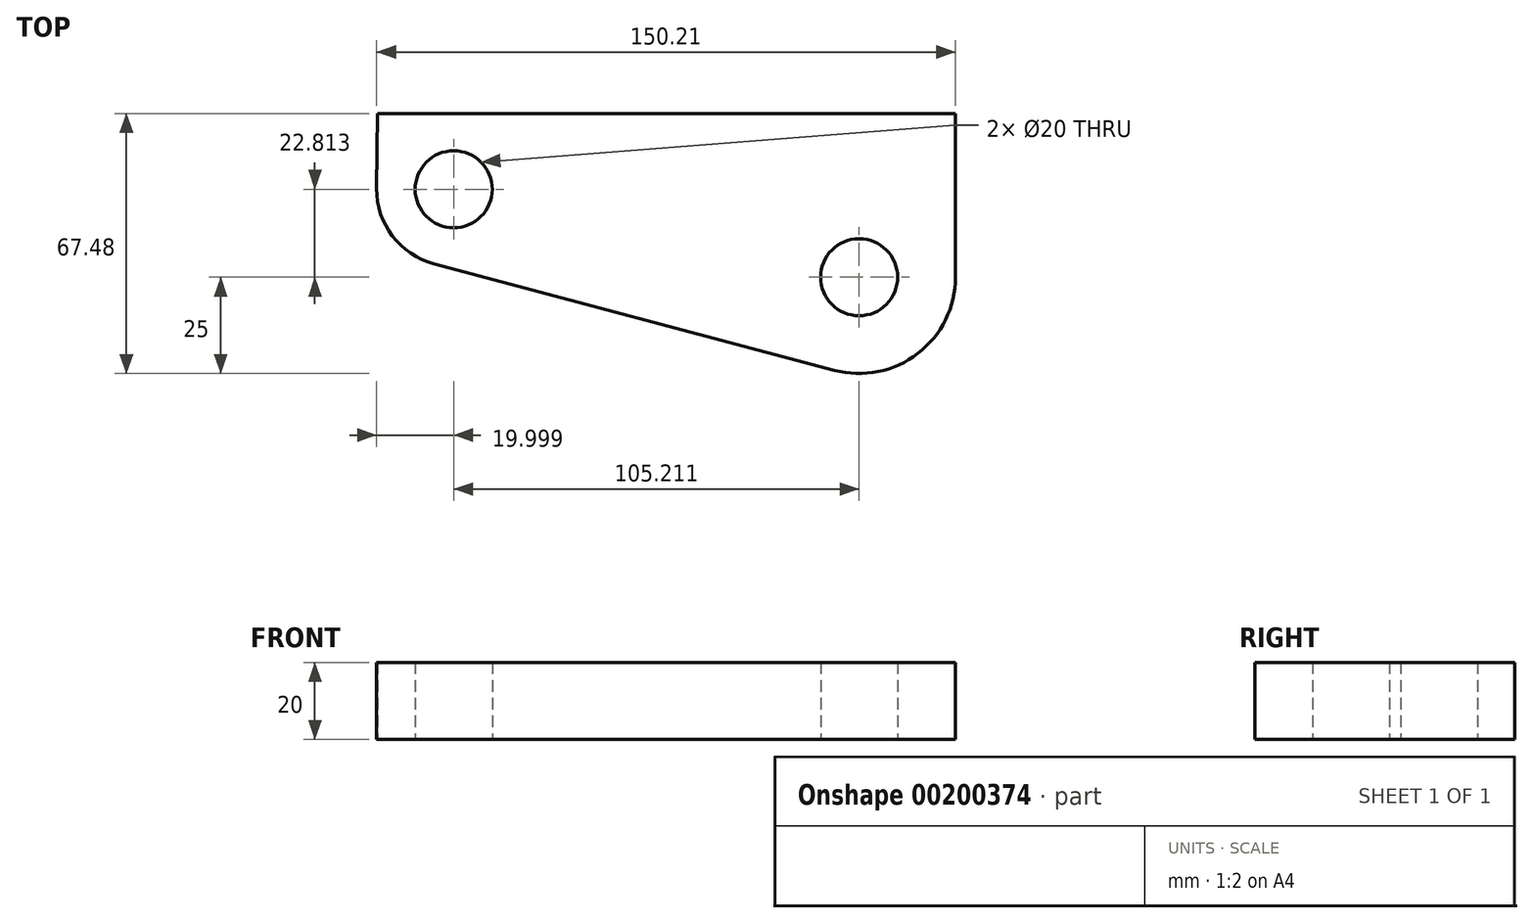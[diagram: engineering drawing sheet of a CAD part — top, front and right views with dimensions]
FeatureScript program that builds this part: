
annotation { "Feature Type Name" : "Feature", "Feature Type Description" : "" }
export const myFeature = defineFeature(function(context is Context, id is Id, definition is map)
    precondition{}
    {
        {
            var Q0;
            Q0=qCreatedBy(makeId("Top.planeOp"),FACE);
            var sketch = newSketch(context, id + "F0", { "sketchPlane" : qUnion([Q0])});
            skLineSegment(sketch, "E0", {"start": v(0, 0) * mm, "end": v(-150, 0) * mm});
            skLineSegment(sketch, "E1", {"start": v(0, 0) * mm, "end": v(0, -42.48) * mm});
            skLineSegment(sketch, "E2", {"start": v(-150, 0) * mm, "end": v(-150.2, -19.45) * mm});
            skLineSegment(sketch, "E3", {"start": v(-135.35, -39) * mm, "end": v(-31.43, -66.64) * mm});
            skPoint(sketch, "E4.visualSharp", {"position": v(-150.38, -35) * mm});
            skArc(sketch, "E4.filletArc", {"start": v(-150.2, -19.45) * mm, "mid": v(-146.13, -31.77) * mm, "end": v(-135.35, -39) * mm});
            skPoint(sketch, "E5.visualSharp", {"position": v(0, -75) * mm});
            skArc(sketch, "E5.filletArc", {"start": v(-31.43, -66.64) * mm, "mid": v(-9.76, -62.3) * mm, "end": v(0, -42.48) * mm});
            skCircle(sketch, "E6", {"center": v(-130.21, -19.67) * mm, "radius": 10 * mm});
            skCircle(sketch, "E7", {"center": v(-25, -42.48) * mm, "radius": 10 * mm});
            skSolve(sketch);
        }
        {
            var Q0;
            Q0 = qSketchRegion(id + "F0", true);
            extrude(context, id + "F1", {"entities" : qUnion([Q0]), "depth" : 20 * mm});
        }
    });
